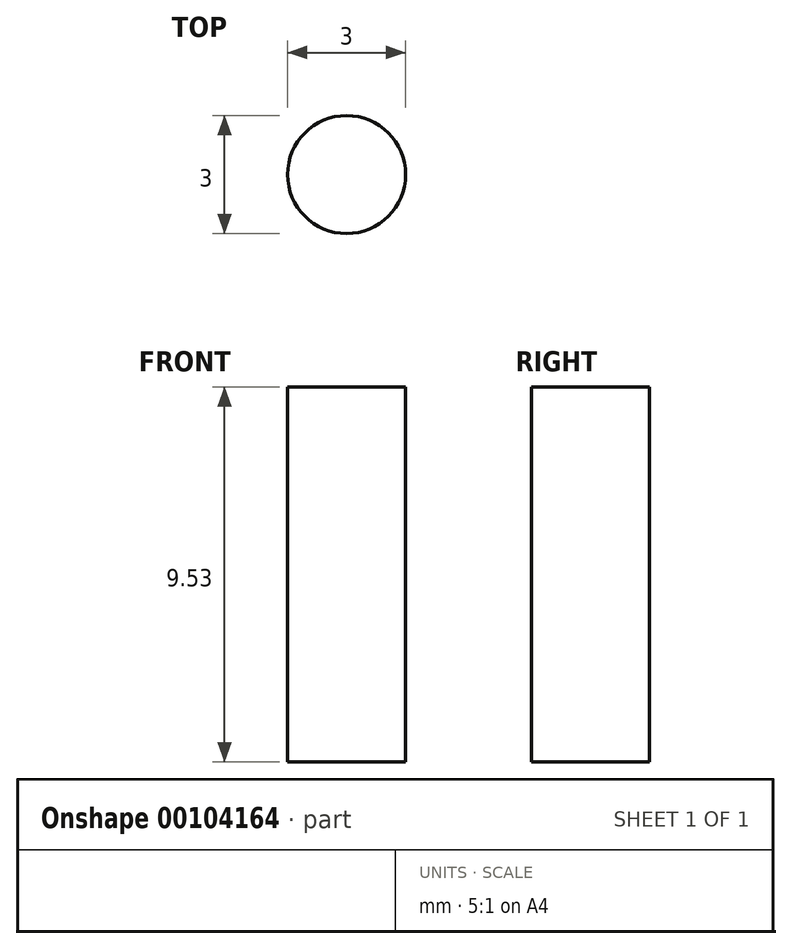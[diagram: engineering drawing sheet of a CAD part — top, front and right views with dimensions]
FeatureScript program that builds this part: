
annotation { "Feature Type Name" : "Feature", "Feature Type Description" : "" }
export const myFeature = defineFeature(function(context is Context, id is Id, definition is map)
    precondition{}
    {
        {
            var Q0;
            Q0=qCreatedBy(makeId("Top.planeOp"),FACE);
            var sketch = newSketch(context, id + "F0", { "sketchPlane" : qUnion([Q0])});
            skCircle(sketch, "E0", {"center": v(-52.28, -17.26) * mm, "radius": 1.5 * mm});
            skSolve(sketch);
        }
        {
            var Q0;
            Q0=makeQuery(id+"F0.imprint","IMPRINT",FACE,{"disambiguationData":[TD([[makeQuery(id+"F0.imprint","IMPRINT",EDGE,{"derivedFrom":sQuery(id+"F0.wireOp",EDGE,"E0")}),1.0]])]});
            extrude(context, id + "F1", {"entities" : qUnion([Q0]), "depth" : 9.52 * mm});
        }
    });
